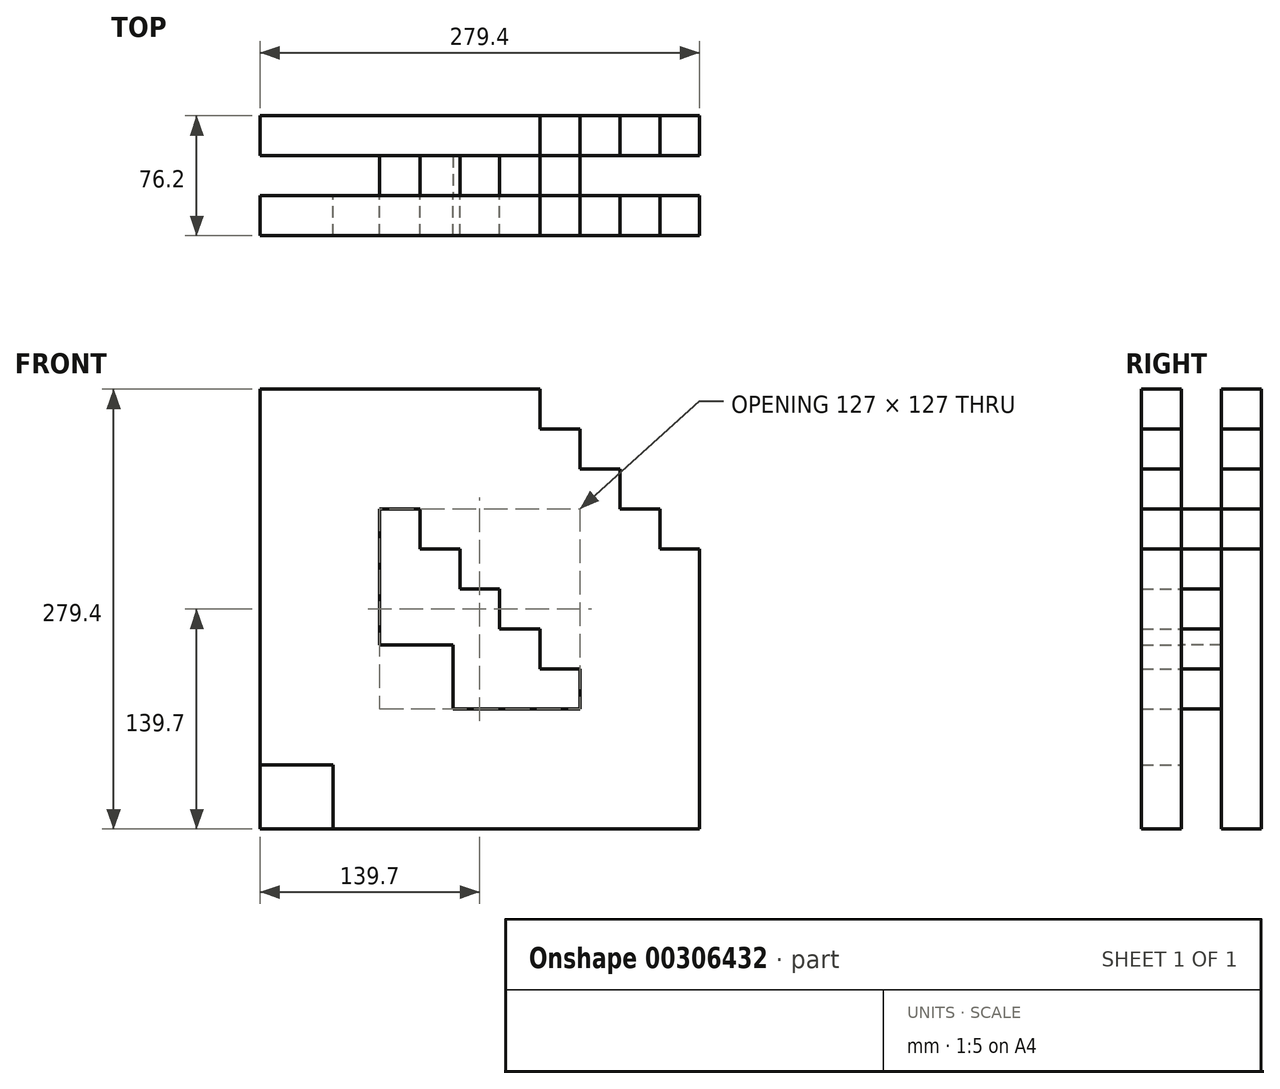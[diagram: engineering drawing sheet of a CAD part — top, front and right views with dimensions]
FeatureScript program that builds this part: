
annotation { "Feature Type Name" : "Feature", "Feature Type Description" : "" }
export const myFeature = defineFeature(function(context is Context, id is Id, definition is map)
    precondition{}
    {
        {
            var Q0;
            Q0=qCreatedBy(makeId("Front.planeOp"),FACE);
            var sketch = newSketch(context, id + "F0", { "sketchPlane" : qUnion([Q0])});
            skLineSegment(sketch, "E0", {"start": v(-76.2, 76.2) * mm, "end": v(-76.2, -50.8) * mm});
            skLineSegment(sketch, "E1", {"start": v(-76.2, -50.8) * mm, "end": v(50.8, -50.8) * mm});
            skLineSegment(sketch, "E2", {"start": v(50.8, -50.8) * mm, "end": v(50.8, -25.4) * mm});
            skLineSegment(sketch, "E3", {"start": v(25.4, -25.4) * mm, "end": v(25.4, 0) * mm});
            skLineSegment(sketch, "E4", {"start": v(25.4, 0) * mm, "end": v(0, 0) * mm});
            skLineSegment(sketch, "E5", {"start": v(0, 0) * mm, "end": v(0, 25.4) * mm});
            skLineSegment(sketch, "E6", {"start": v(0, 25.4) * mm, "end": v(-25.4, 25.4) * mm});
            skLineSegment(sketch, "E7", {"start": v(-25.4, 25.4) * mm, "end": v(-25.4, 50.8) * mm});
            skLineSegment(sketch, "E8", {"start": v(-50.8, 50.8) * mm, "end": v(-50.8, 67.5) * mm});
            skLineSegment(sketch, "E9", {"start": v(-50.8, 67.5) * mm, "end": v(-50.8, 76.2) * mm});
            skLineSegment(sketch, "E10", {"start": v(-50.8, 76.2) * mm, "end": v(-76.2, 76.2) * mm});
            skLineSegment(sketch, "E11", {"start": v(-50.8, 50.8) * mm, "end": v(-25.4, 50.8) * mm});
            skLineSegment(sketch, "E12", {"start": v(25.4, -25.4) * mm, "end": v(50.8, -25.4) * mm});
            skSolve(sketch);
        }
        {
            var Q0;
            Q0 = qSketchRegion(id + "F0", true);
            var Q1;
            Q1=makeQuery(id+"F0.imprint","IMPRINT",FACE,{"disambiguationData":[TD([[makeQuery(id+"F0.imprint","IMPRINT",EDGE,{"derivedFrom":sQuery(id+"F0.wireOp",EDGE,"E0")}),1.0]])]});
            extrude(context, id + "F1", {"entities" : qUnion([Q0, Q1]), "depth" : 50.8 * mm});
        }
        {
            var Q0;
            Q0=makeQuery(id+"F1.opExtrude","CAP_FACE",FACE,{"disambiguationData":[OSD([sQuery(id+"F0.wireOp",EDGE,"E0"),sQuery(id+"F0.wireOp",EDGE,"E1"),sQuery(id+"F0.wireOp",EDGE,"E2"),sQuery(id+"F0.wireOp",EDGE,"E3"),sQuery(id+"F0.wireOp",EDGE,"E4"),sQuery(id+"F0.wireOp",EDGE,"E5"),sQuery(id+"F0.wireOp",EDGE,"E6"),sQuery(id+"F0.wireOp",EDGE,"E7"),sQuery(id+"F0.wireOp",EDGE,"E8"),sQuery(id+"F0.wireOp",EDGE,"E9"),sQuery(id+"F0.wireOp",EDGE,"E10"),sQuery(id+"F0.wireOp",EDGE,"E11"),sQuery(id+"F0.wireOp",EDGE,"E12")])],"isStart":false});
            var sketch = newSketch(context, id + "F2", { "sketchPlane" : qUnion([Q0])});
            skLineSegment(sketch, "E13", {"start": v(-76.2, -10.06) * mm, "end": v(-29.73, -10.06) * mm});
            skLineSegment(sketch, "E14", {"start": v(-29.73, -10.06) * mm, "end": v(-29.73, -50.8) * mm});
            skSolve(sketch);
        }
        {
            var Q0;
            Q0 = qSketchRegion(id + "F2", true);
            var Q1;
            {var subQ0=sQuery(id+"F2.wireOp",EDGE,"E13");Q1=makeQuery(id+"F2.imprint","IMPRINT",FACE,{"disambiguationData":[TD([[makeQuery(id+"F2.imprint","IMPRINT",EDGE,{"derivedFrom":subQ0}),-1.0]])]});}
            extrude(context, id + "F3", {"entities" : qUnion([Q0, Q1]), "operationType" : NewBodyOperationType.REMOVE, "oppositeDirection" : true, "depth" : 25.4 * mm});
        }
        {
            var Q0;
            Q0=makeQuery(id+"F0.imprint","IMPRINT",FACE,{"disambiguationData":[TD([[makeQuery(id+"F0.imprint","IMPRINT",EDGE,{"derivedFrom":sQuery(id+"F0.wireOp",EDGE,"E0")}),1.0]])]});
            var sketch = newSketch(context, id + "F4", { "sketchPlane" : qUnion([Q0])});
            skLineSegment(sketch, "E15.0", {"start": v(50.8, 101.6) * mm, "end": v(50.8, 127) * mm});
            skLineSegment(sketch, "E15.1", {"start": v(-152.4, -127) * mm, "end": v(127, -127) * mm});
            skLineSegment(sketch, "E15.2", {"start": v(-152.4, 152.4) * mm, "end": v(-152.4, -127) * mm});
            skLineSegment(sketch, "E15.3", {"start": v(25.4, 152.4) * mm, "end": v(-152.4, 152.4) * mm});
            skLineSegment(sketch, "E15.4", {"start": v(25.4, 127) * mm, "end": v(25.4, 152.4) * mm});
            skLineSegment(sketch, "E15.5", {"start": v(127, -127) * mm, "end": v(127, 50.8) * mm});
            skLineSegment(sketch, "E15.6", {"start": v(50.8, 127) * mm, "end": v(25.4, 127) * mm});
            skLineSegment(sketch, "E15.7", {"start": v(127, 50.8) * mm, "end": v(101.6, 50.8) * mm});
            skLineSegment(sketch, "E15.8", {"start": v(101.6, 50.8) * mm, "end": v(101.6, 76.2) * mm});
            skLineSegment(sketch, "E15.9", {"start": v(101.6, 76.2) * mm, "end": v(76.2, 76.2) * mm});
            skLineSegment(sketch, "E15.10", {"start": v(76.2, 76.2) * mm, "end": v(76.2, 101.6) * mm});
            skLineSegment(sketch, "E15.11", {"start": v(76.2, 101.6) * mm, "end": v(50.8, 101.6) * mm});
            skSolve(sketch);
        }
        {
            var Q0;
            Q0 = qSketchRegion(id + "F4", true);
            var Q1;
            Q1=makeQuery(id+"F4.imprint","IMPRINT",FACE,{"disambiguationData":[TD([[makeQuery(id+"F4.imprint","IMPRINT",EDGE,{"derivedFrom":sQuery(id+"F4.wireOp",EDGE,"E15.0")}),1.0]])]});
            extrude(context, id + "F5", {"entities" : qUnion([Q0, Q1]), "operationType" : NewBodyOperationType.ADD, "depth" : 25.4 * mm});
        }
        {
            var Q0;
            Q0=makeQuery(id+"F1.opExtrude","CAP_FACE",FACE,{"disambiguationData":[OSD([sQuery(id+"F0.wireOp",EDGE,"E0"),sQuery(id+"F0.wireOp",EDGE,"E1"),sQuery(id+"F0.wireOp",EDGE,"E2"),sQuery(id+"F0.wireOp",EDGE,"E3"),sQuery(id+"F0.wireOp",EDGE,"E4"),sQuery(id+"F0.wireOp",EDGE,"E5"),sQuery(id+"F0.wireOp",EDGE,"E6"),sQuery(id+"F0.wireOp",EDGE,"E7"),sQuery(id+"F0.wireOp",EDGE,"E8"),sQuery(id+"F0.wireOp",EDGE,"E9"),sQuery(id+"F0.wireOp",EDGE,"E10"),sQuery(id+"F0.wireOp",EDGE,"E11"),sQuery(id+"F0.wireOp",EDGE,"E12")])],"isStart":false});
            var sketch = newSketch(context, id + "F6", { "sketchPlane" : qUnion([Q0])});
            skLineSegment(sketch, "E16.0", {"start": v(-152.4, 152.4) * mm, "end": v(-152.4, -86.26) * mm});
            skLineSegment(sketch, "E16.1", {"start": v(25.4, 152.4) * mm, "end": v(-152.4, 152.4) * mm});
            skLineSegment(sketch, "E16.2", {"start": v(25.4, 127) * mm, "end": v(25.4, 152.4) * mm});
            skLineSegment(sketch, "E16.3", {"start": v(127, 50.8) * mm, "end": v(101.6, 50.8) * mm});
            skLineSegment(sketch, "E16.4", {"start": v(127, -127) * mm, "end": v(127, 50.8) * mm});
            skLineSegment(sketch, "E16.5", {"start": v(-105.93, -127) * mm, "end": v(127, -127) * mm});
            skLineSegment(sketch, "E16.6", {"start": v(-105.93, -86.26) * mm, "end": v(-105.93, -127) * mm});
            skLineSegment(sketch, "E16.7", {"start": v(101.6, 50.8) * mm, "end": v(101.6, 76.2) * mm});
            skLineSegment(sketch, "E16.8", {"start": v(101.6, 76.2) * mm, "end": v(76.2, 76.2) * mm});
            skLineSegment(sketch, "E16.9", {"start": v(76.2, 76.2) * mm, "end": v(76.2, 101.6) * mm});
            skLineSegment(sketch, "E16.10", {"start": v(-152.4, -86.26) * mm, "end": v(-105.93, -86.26) * mm});
            skLineSegment(sketch, "E16.11", {"start": v(76.2, 101.6) * mm, "end": v(50.8, 101.6) * mm});
            skLineSegment(sketch, "E16.12", {"start": v(50.8, 101.6) * mm, "end": v(50.8, 127) * mm});
            skLineSegment(sketch, "E16.13", {"start": v(50.8, 127) * mm, "end": v(25.4, 127) * mm});
            skSolve(sketch);
        }
        {
            var Q0;
            Q0=makeQuery(id+"F6.imprint","IMPRINT",FACE,{"disambiguationData":[TD([[makeQuery(id+"F6.imprint","IMPRINT",EDGE,{"derivedFrom":sQuery(id+"F6.wireOp",EDGE,"E16.0")}),1.0]])]});
            extrude(context, id + "F7", {"entities" : qUnion([Q0]), "depth" : 25.4 * mm});
        }
    });
